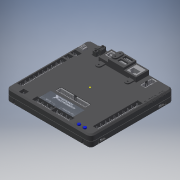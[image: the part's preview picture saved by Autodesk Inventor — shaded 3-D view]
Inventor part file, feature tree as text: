
AUTODESK INVENTOR PART (.ipt)
format: ipt  version: 2016 (Build 200138000, 138)  size: 39,043,072 bytes
history: native  units: in
note: dims shown in document units (in); Inventor stores cm internally (conversion verified against a paired STEP export)
features: imported_body x16, other x3, sketch x2, plane x1
ambient origin geometry x8: Origin, YZ Plane, XZ Plane, XY Plane, X Axis, Y Axis, Z Axis, Center Point
bodies: Solid1 (feature_tree), Solid2 (feature_tree), Solid3 (feature_tree), Solid4 (feature_tree), Solid5 (feature_tree), Solid6 (feature_tree), Solid7 (feature_tree), Solid8 (feature_tree), Solid9 (feature_tree), Solid10 (feature_tree), Solid11 (feature_tree), Solid12 (feature_tree), Solid13 (feature_tree), Solid14 (feature_tree), Solid15 (feature_tree), Solid16 (feature_tree)
feature tree (22):
  other  "cd_roborio1"
  sketch  "Sketch1"
  other  "Decal2"
  plane  "Work Plane1"
  imported_body  "Base1"
  imported_body  "Base2"
  imported_body  "Base3"
  imported_body  "Base4"
  imported_body  "Base5"
  imported_body  "Base6"
  imported_body  "Base7"
  imported_body  "Base8"
  imported_body  "Base9"
  imported_body  "Base10"
  imported_body  "Base11"
  imported_body  "Base12"
  imported_body  "Base13"
  imported_body  "Base14"
  imported_body  "Base15"
  imported_body  "Base16"
  sketch  "Sketch3"
  other  "Image2"
